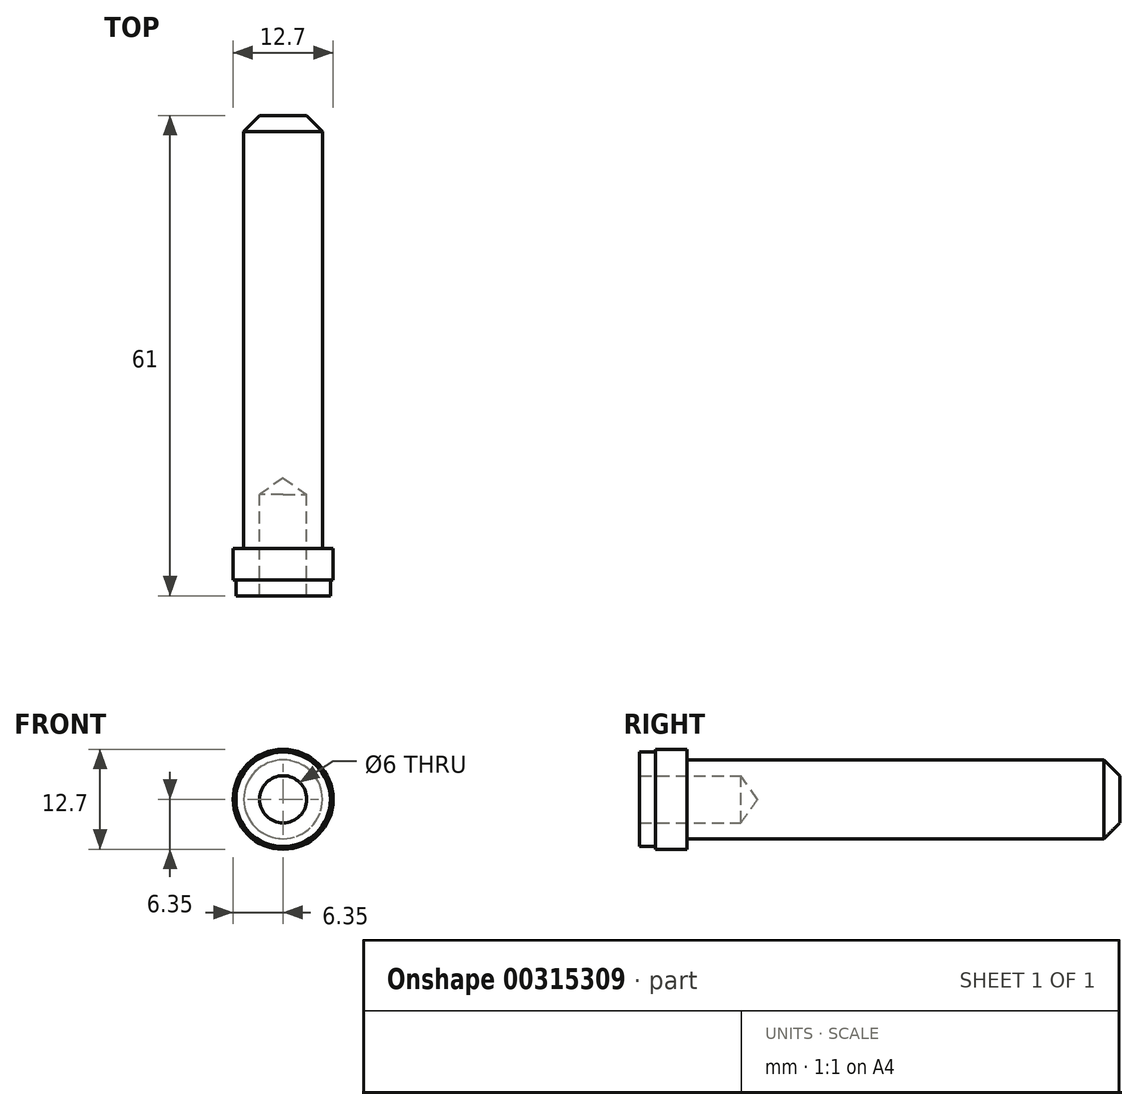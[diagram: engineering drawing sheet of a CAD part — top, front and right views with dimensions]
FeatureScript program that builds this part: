
annotation { "Feature Type Name" : "Feature", "Feature Type Description" : "" }
export const myFeature = defineFeature(function(context is Context, id is Id, definition is map)
    precondition{}
    {
        {
            var Q0;
            Q0=qCreatedBy(makeId("Right.planeOp"),FACE);
            var sketch = newSketch(context, id + "F0", { "sketchPlane" : qUnion([Q0])});
            skLineSegment(sketch, "E0", {"start": v(-5.85, -6) * mm, "end": v(-5.85, -6.35) * mm});
            skLineSegment(sketch, "E1", {"start": v(-5.85, -6.35) * mm, "end": v(-1.85, -6.35) * mm});
            skLineSegment(sketch, "E2", {"start": v(-1.85, -6.35) * mm, "end": v(-1.85, -5) * mm});
            skLineSegment(sketch, "E3", {"start": v(-1.85, -5) * mm, "end": v(53.15, -5) * mm});
            skLineSegment(sketch, "E4", {"start": v(53.15, -5) * mm, "end": v(53.15, 0) * mm});
            skLineSegment(sketch, "E5", {"start": v(53.15, 0) * mm, "end": v(7.15, 0) * mm});
            skPoint(sketch, "E6.start.orphan", {"position": v(2.15, -5.5) * mm});
            skLineSegment(sketch, "E7", {"start": v(-7.85, -3) * mm, "end": v(5, -3) * mm});
            skLineSegment(sketch, "E8", {"start": v(5, -3) * mm, "end": v(7.15, 0) * mm});
            skLineSegment(sketch, "E9", {"start": v(-7.85, -3) * mm, "end": v(-7.85, -5.5) * mm});
            skPoint(sketch, "E10.end.orphan", {"position": v(-0.35, -5.5) * mm});
            skLineSegment(sketch, "E11", {"start": v(-5.85, -6) * mm, "end": v(-7.85, -6) * mm});
            skLineSegment(sketch, "E12", {"start": v(-7.85, -6) * mm, "end": v(-7.85, -5.5) * mm});
            skPoint(sketch, "E13.end.orphan", {"position": v(-2.85, -5.5) * mm});
            skLineSegment(sketch, "E14", {"start": v(-1.85, -6.35) * mm, "end": v(45.2, -6.35) * mm});
            skLineSegment(sketch, "E15", {"start": v(45.2, -6.35) * mm, "end": v(45.2, -5) * mm});
            skSolve(sketch);
        }
        {
            var Q0;
            Q0=makeQuery(id+"F0.imprint","IMPRINT",FACE,{"disambiguationData":[TD([[makeQuery(id+"F0.imprint","IMPRINT",EDGE,{"derivedFrom":sQuery(id+"F0.wireOp",EDGE,"E0")}),1.0]])]});
            var Q1;
            Q1=makeQuery(id+"F0.imprint","IMPRINT",FACE,{"disambiguationData":[TD([[makeQuery(id+"F0.imprint","IMPRINT",EDGE,{"derivedFrom":sQuery(id+"F0.wireOp",EDGE,"E13")}),-1.0]])]});
            var Q2;
            Q2=sQuery(id+"F0.wireOp",EDGE,"E5");
            revolve(context, id + "F1", {"entities" : qUnion([Q0, Q1]), "axis" : qUnion([Q2]), "revolveType" : RevolveType.FULL, "surfaceOperationType" : NewSurfaceOperationType.NEW});
        }
        {
            var Q0;
            Q0=makeQuery(id+"F1.opRevolve","SWEPT_FACE",FACE,{"disambiguationData":[OSD([sQuery(id+"F0.wireOp",EDGE,"E4")])]});
            var sketch = newSketch(context, id + "F2", { "sketchPlane" : qUnion([Q0])});
            skCircle(sketch, "E16", {"center": v(0, 0) * mm, "radius": 4 * mm});
            skLineSegment(sketch, "E17.bottom", {"start": v(-4, -4) * mm, "end": v(4, -4) * mm});
            skLineSegment(sketch, "E17.top", {"start": v(-4, 4) * mm, "end": v(4, 4) * mm});
            skLineSegment(sketch, "E17.left", {"start": v(-4, -4) * mm, "end": v(-4, 4) * mm});
            skLineSegment(sketch, "E17.right", {"start": v(4, -4) * mm, "end": v(4, 4) * mm});
            skLineSegment(sketch, "E18", {"start": v(-4, 0) * mm, "end": v(-4, 4) * mm});
            skLineSegment(sketch, "E19", {"start": v(-4, 4) * mm, "end": v(-4, 0) * mm});
            skLineSegment(sketch, "E20", {"start": v(-4, 0) * mm, "end": v(-4, -4) * mm});
            skCircle(sketch, "E21", {"center": v(0, 0) * mm, "radius": 5 * mm});
            skSolve(sketch);
        }
        {
            var Q0;
            Q0=makeQuery(id+"F1.opRevolve","SWEPT_EDGE",EDGE,{"disambiguationData":[OSD([sQuery(id+"F0.wireOp",EDGE,"E3"),sQuery(id+"F0.wireOp",EDGE,"E4")])]});
            chamfer(context, id + "F3", {"entities" : qUnion([Q0]), "chamferType" : ChamferType.TWO_OFFSETS, "width1" : 2 * mm, "oppositeDirection" : false, "width2" : 2 * mm, "tangentPropagation" : true});
        }
    });
